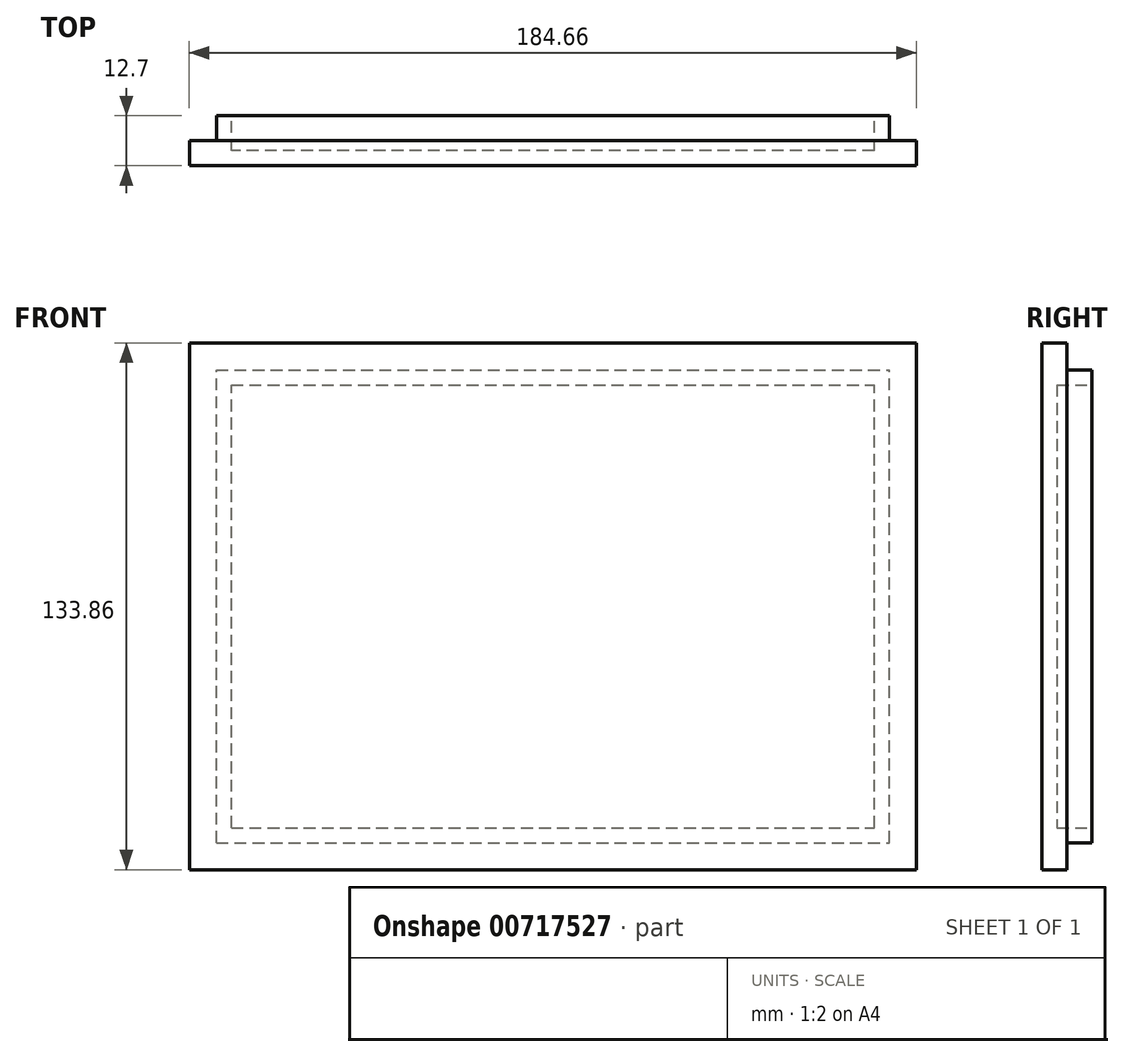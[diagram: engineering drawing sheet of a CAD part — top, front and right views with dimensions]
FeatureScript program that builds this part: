
annotation { "Feature Type Name" : "Feature", "Feature Type Description" : "" }
export const myFeature = defineFeature(function(context is Context, id is Id, definition is map)
    precondition{}
    {
        {
            var Q0;
            Q0=qCreatedBy(makeId("Front.planeOp"),FACE);
            var sketch = newSketch(context, id + "F0", { "sketchPlane" : qUnion([Q0])});
            skLineSegment(sketch, "E0.bottom", {"start": v(0, 0) * mm, "end": v(170.94, 0) * mm});
            skLineSegment(sketch, "E0.top", {"start": v(0, 120.14) * mm, "end": v(170.94, 120.14) * mm});
            skLineSegment(sketch, "E0.left", {"start": v(0, 0) * mm, "end": v(0, 120.14) * mm});
            skLineSegment(sketch, "E0.right", {"start": v(170.94, 0) * mm, "end": v(170.94, 120.14) * mm});
            skSolve(sketch);
        }
        {
            var Q0;
            Q0=makeQuery(id+"F0.imprint","IMPRINT",FACE,{"disambiguationData":[TD([[makeQuery(id+"F0.imprint","IMPRINT",EDGE,{"derivedFrom":sQuery(id+"F0.wireOp",EDGE,"E0.bottom")}),1.0]])]});
            extrude(context, id + "F1", {"entities" : qUnion([Q0]), "depth" : 12.7 * mm, "offsetDistance" : 25.4 * mm});
        }
        {
            var Q0;
            Q0=makeQuery(id+"F1.opExtrude","CAP_FACE",FACE,{"disambiguationData":[OSD([sQuery(id+"F0.wireOp",EDGE,"E0.bottom"),sQuery(id+"F0.wireOp",EDGE,"E0.top"),sQuery(id+"F0.wireOp",EDGE,"E0.left"),sQuery(id+"F0.wireOp",EDGE,"E0.right")])],"isStart":false});
            var sketch = newSketch(context, id + "F2", { "sketchPlane" : qUnion([Q0])});
            skLineSegment(sketch, "E1.bottom", {"start": v(-6.86, -6.86) * mm, "end": v(177.8, -6.86) * mm});
            skLineSegment(sketch, "E1.top", {"start": v(-6.86, 127) * mm, "end": v(177.8, 127) * mm});
            skLineSegment(sketch, "E1.left", {"start": v(-6.86, -6.86) * mm, "end": v(-6.86, 127) * mm});
            skLineSegment(sketch, "E1.right", {"start": v(177.8, -6.86) * mm, "end": v(177.8, 127) * mm});
            skSolve(sketch);
        }
        {
            var Q0;
            Q0=makeQuery(id+"F2.imprint","IMPRINT",FACE,{"disambiguationData":[TD([[makeQuery(id+"F2.imprint","IMPRINT",EDGE,{"derivedFrom":sQuery(id+"F2.wireOp",EDGE,"E1.bottom")}),1.0]])]});
            extrude(context, id + "F3", {"entities" : qUnion([Q0]), "operationType" : NewBodyOperationType.ADD, "oppositeDirection" : true, "depth" : 6.35 * mm, "offsetDistance" : 25.4 * mm});
        }
        {
            var Q0;
            Q0=makeQuery(id+"F1.opExtrude","CAP_FACE",FACE,{"disambiguationData":[OSD([sQuery(id+"F0.wireOp",EDGE,"E0.bottom"),sQuery(id+"F0.wireOp",EDGE,"E0.top"),sQuery(id+"F0.wireOp",EDGE,"E0.left"),sQuery(id+"F0.wireOp",EDGE,"E0.right")])],"isStart":true});
            shell(context, id + "F4", {"entities" : qUnion([Q0]), "thickness" : 3.8 * mm});
        }
    });
